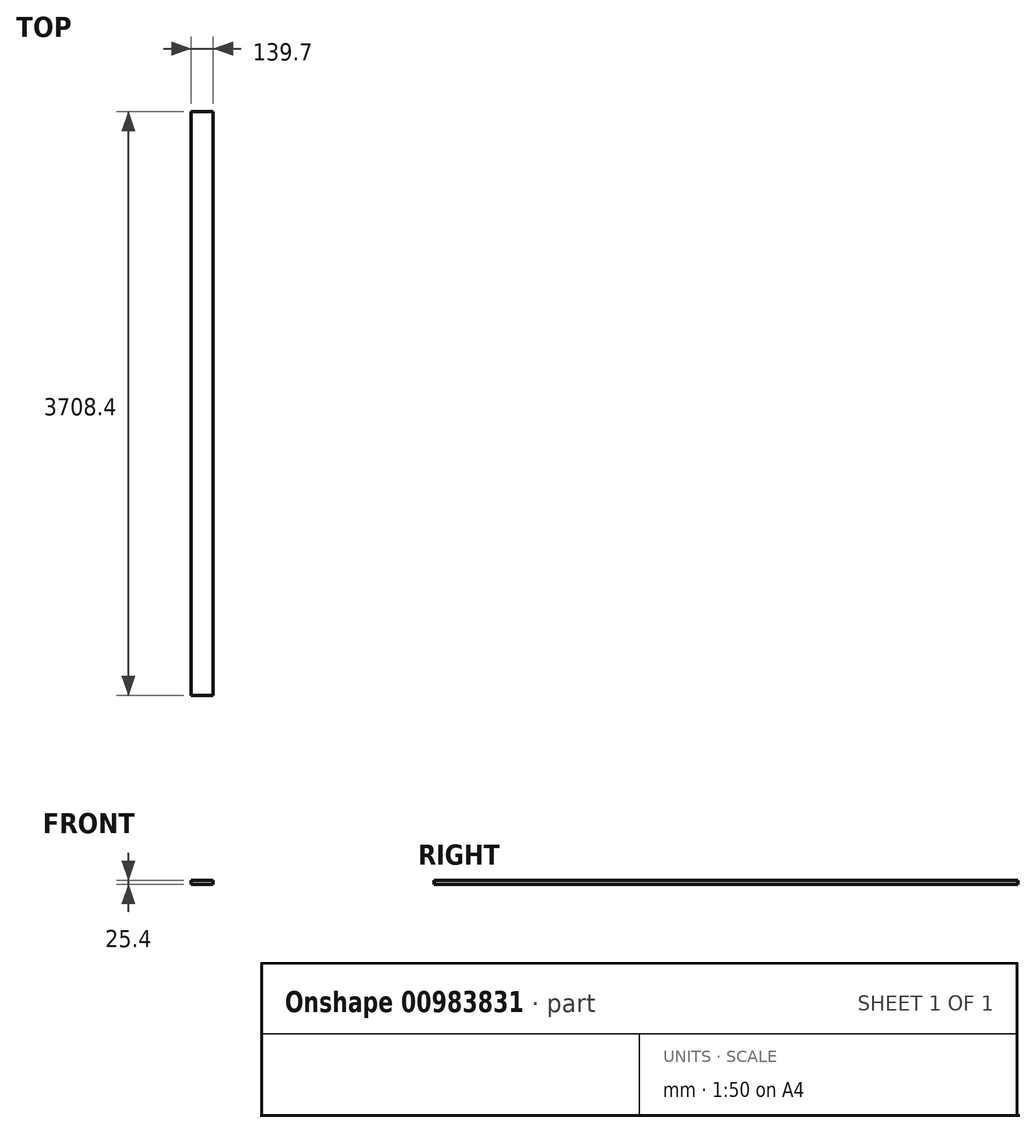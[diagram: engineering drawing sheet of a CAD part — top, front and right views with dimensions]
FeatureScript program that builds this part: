
annotation { "Feature Type Name" : "Feature", "Feature Type Description" : "" }
export const myFeature = defineFeature(function(context is Context, id is Id, definition is map)
    precondition{}
    {
        {
            var Q0;
            Q0=qCreatedBy(makeId("Front.planeOp"),FACE);
            var sketch = newSketch(context, id + "F0", { "sketchPlane" : qUnion([Q0])});
            skLineSegment(sketch, "E0.bottom", {"start": v(0, 0) * mm, "end": v(139.7, 0) * mm});
            skLineSegment(sketch, "E0.top", {"start": v(0, 25.4) * mm, "end": v(139.7, 25.4) * mm});
            skLineSegment(sketch, "E0.left", {"start": v(0, 0) * mm, "end": v(0, 25.4) * mm});
            skLineSegment(sketch, "E0.right", {"start": v(139.7, 0) * mm, "end": v(139.7, 25.4) * mm});
            skSolve(sketch);
        }
        {
            var Q0;
            Q0=makeQuery(id+"F0.imprint","IMPRINT",FACE,{"disambiguationData":[TD([[makeQuery(id+"F0.imprint","IMPRINT",EDGE,{"derivedFrom":sQuery(id+"F0.wireOp",EDGE,"E0.bottom")}),1.0]])]});
            extrude(context, id + "F1", {"entities" : qUnion([Q0]), "depth" : 3708.4 * mm, "offsetDistance" : 25.4 * mm});
        }
    });
